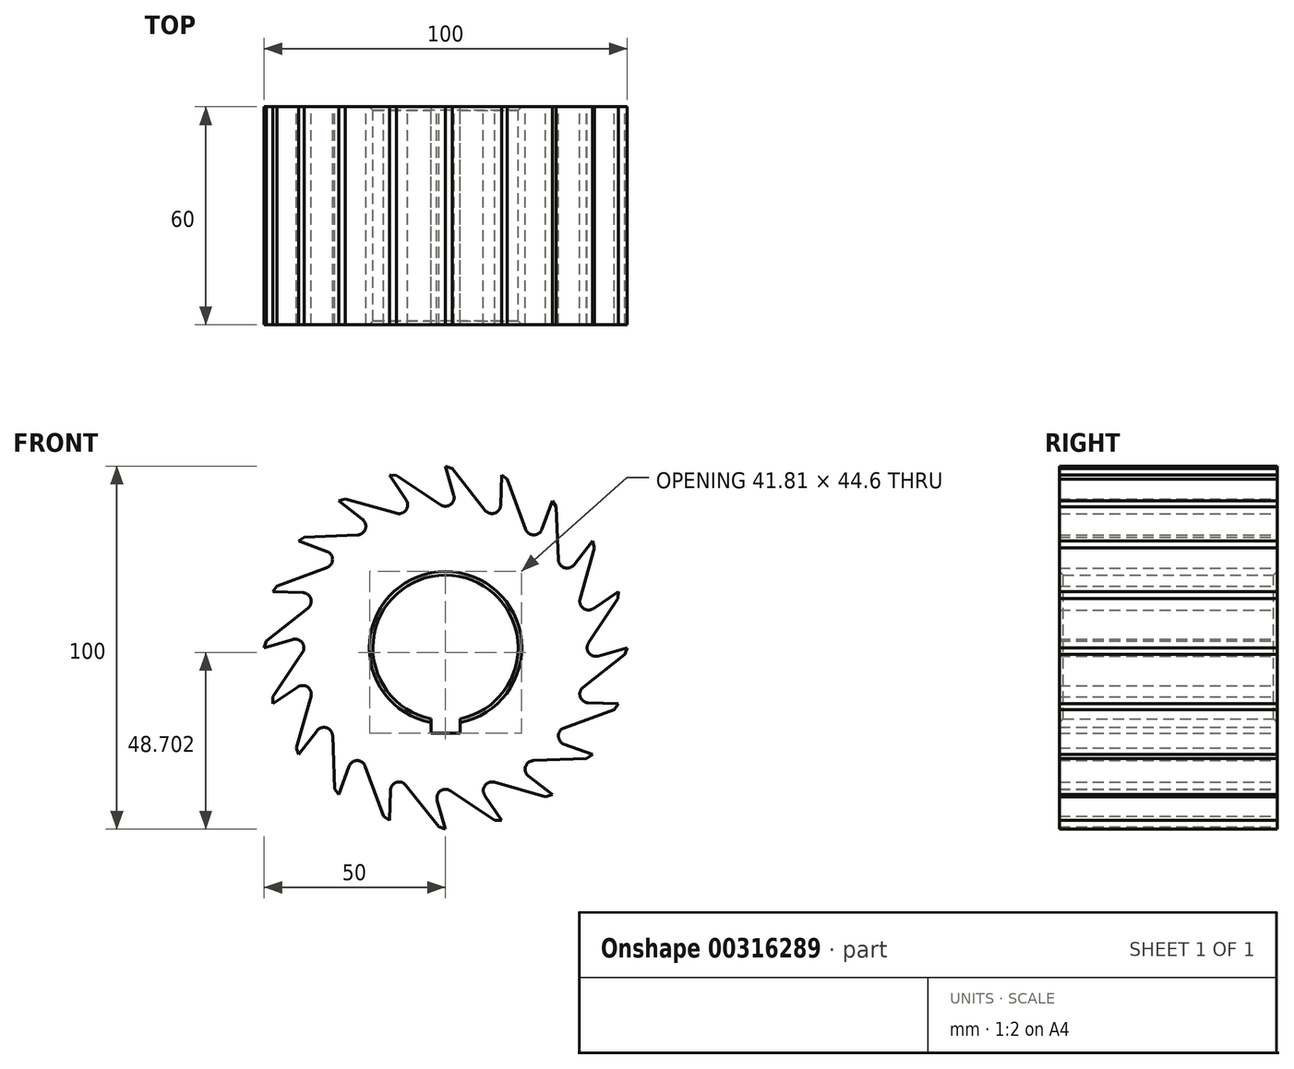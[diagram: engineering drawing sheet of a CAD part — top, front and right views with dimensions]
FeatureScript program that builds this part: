
annotation { "Feature Type Name" : "Feature", "Feature Type Description" : "" }
export const myFeature = defineFeature(function(context is Context, id is Id, definition is map)
    precondition{}
    {
        {
            var Q0;
            Q0=qCreatedBy(makeId("Front.planeOp"),FACE);
            var sketch = newSketch(context, id + "F0", { "sketchPlane" : qUnion([Q0])});
            skLineSegment(sketch, "E0", {"start": v(0, 50) * mm, "end": v(2.29, 42.02) * mm});
            skLineSegment(sketch, "E1", {"start": v(0, 50) * mm, "end": v(1.83, 49.37) * mm});
            skArc(sketch, "E2.19.0", {"start": v(10.91, 37.86) * mm, "mid": v(13.52, 37.08) * mm, "end": v(15.16, 39.26) * mm});
            skLineSegment(sketch, "E3.19.0", {"start": v(1.83, 49.37) * mm, "end": v(10.91, 37.86) * mm});
            skArc(sketch, "E4.1.0", {"start": v(-1.32, 39.38) * mm, "mid": v(1.4, 39.44) * mm, "end": v(2.29, 42.02) * mm});
            skLineSegment(sketch, "E4.1.1", {"start": v(-13.52, 47.52) * mm, "end": v(-1.32, 39.38) * mm});
            skLineSegment(sketch, "E4.1.2", {"start": v(-15.45, 47.55) * mm, "end": v(-10.8, 40.67) * mm});
            skLineSegment(sketch, "E4.1.3", {"start": v(-15.45, 47.55) * mm, "end": v(-13.52, 47.52) * mm});
            skArc(sketch, "E4.2.0", {"start": v(-13.43, 37.05) * mm, "mid": v(-10.85, 37.94) * mm, "end": v(-10.8, 40.67) * mm});
            skLineSegment(sketch, "E4.2.1", {"start": v(-27.54, 41.02) * mm, "end": v(-13.43, 37.05) * mm});
            skLineSegment(sketch, "E4.2.2", {"start": v(-29.39, 40.45) * mm, "end": v(-22.85, 35.34) * mm});
            skLineSegment(sketch, "E4.2.3", {"start": v(-29.39, 40.45) * mm, "end": v(-27.54, 41.02) * mm});
            skArc(sketch, "E4.3.0", {"start": v(-24.22, 31.09) * mm, "mid": v(-22.05, 32.73) * mm, "end": v(-22.85, 35.34) * mm});
            skLineSegment(sketch, "E4.3.1", {"start": v(-38.87, 30.5) * mm, "end": v(-24.22, 31.09) * mm});
            skLineSegment(sketch, "E4.3.2", {"start": v(-40.45, 29.39) * mm, "end": v(-32.65, 26.55) * mm});
            skLineSegment(sketch, "E4.3.3", {"start": v(-40.45, 29.39) * mm, "end": v(-38.87, 30.5) * mm});
            skArc(sketch, "E4.4.0", {"start": v(-32.64, 22.08) * mm, "mid": v(-31.08, 24.32) * mm, "end": v(-32.65, 26.55) * mm});
            skLineSegment(sketch, "E4.4.1", {"start": v(-46.39, 17) * mm, "end": v(-32.64, 22.08) * mm});
            skLineSegment(sketch, "E4.4.2", {"start": v(-47.55, 15.45) * mm, "end": v(-39.26, 15.16) * mm});
            skLineSegment(sketch, "E4.4.3", {"start": v(-47.55, 15.45) * mm, "end": v(-46.39, 17) * mm});
            skArc(sketch, "E4.5.0", {"start": v(-37.86, 10.91) * mm, "mid": v(-37.08, 13.52) * mm, "end": v(-39.26, 15.16) * mm});
            skLineSegment(sketch, "E4.5.1", {"start": v(-49.37, 1.83) * mm, "end": v(-37.86, 10.91) * mm});
            skLineSegment(sketch, "E4.5.2", {"start": v(-50, 0) * mm, "end": v(-42.02, 2.29) * mm});
            skLineSegment(sketch, "E4.5.3", {"start": v(-50, 0) * mm, "end": v(-49.37, 1.83) * mm});
            skArc(sketch, "E4.6.0", {"start": v(-39.38, -1.32) * mm, "mid": v(-39.44, 1.4) * mm, "end": v(-42.02, 2.29) * mm});
            skLineSegment(sketch, "E4.6.1", {"start": v(-47.52, -13.52) * mm, "end": v(-39.38, -1.32) * mm});
            skLineSegment(sketch, "E4.6.2", {"start": v(-47.55, -15.45) * mm, "end": v(-40.67, -10.8) * mm});
            skLineSegment(sketch, "E4.6.3", {"start": v(-47.55, -15.45) * mm, "end": v(-47.52, -13.52) * mm});
            skArc(sketch, "E4.7.0", {"start": v(-37.05, -13.43) * mm, "mid": v(-37.94, -10.85) * mm, "end": v(-40.67, -10.8) * mm});
            skLineSegment(sketch, "E4.7.1", {"start": v(-41.02, -27.54) * mm, "end": v(-37.05, -13.43) * mm});
            skLineSegment(sketch, "E4.7.2", {"start": v(-40.45, -29.39) * mm, "end": v(-35.34, -22.85) * mm});
            skLineSegment(sketch, "E4.7.3", {"start": v(-40.45, -29.39) * mm, "end": v(-41.02, -27.54) * mm});
            skArc(sketch, "E4.8.0", {"start": v(-31.09, -24.22) * mm, "mid": v(-32.73, -22.05) * mm, "end": v(-35.34, -22.85) * mm});
            skLineSegment(sketch, "E4.8.1", {"start": v(-30.5, -38.87) * mm, "end": v(-31.09, -24.22) * mm});
            skLineSegment(sketch, "E4.8.2", {"start": v(-29.39, -40.45) * mm, "end": v(-26.55, -32.65) * mm});
            skLineSegment(sketch, "E4.8.3", {"start": v(-29.39, -40.45) * mm, "end": v(-30.5, -38.87) * mm});
            skArc(sketch, "E4.9.0", {"start": v(-22.08, -32.64) * mm, "mid": v(-24.32, -31.08) * mm, "end": v(-26.55, -32.65) * mm});
            skLineSegment(sketch, "E4.9.1", {"start": v(-17, -46.39) * mm, "end": v(-22.08, -32.64) * mm});
            skLineSegment(sketch, "E4.9.2", {"start": v(-15.45, -47.55) * mm, "end": v(-15.16, -39.26) * mm});
            skLineSegment(sketch, "E4.9.3", {"start": v(-15.45, -47.55) * mm, "end": v(-17, -46.39) * mm});
            skArc(sketch, "E4.10.0", {"start": v(-10.91, -37.86) * mm, "mid": v(-13.52, -37.08) * mm, "end": v(-15.16, -39.26) * mm});
            skLineSegment(sketch, "E4.10.1", {"start": v(-1.83, -49.37) * mm, "end": v(-10.91, -37.86) * mm});
            skLineSegment(sketch, "E4.10.2", {"start": v(0, -50) * mm, "end": v(-2.29, -42.02) * mm});
            skLineSegment(sketch, "E4.10.3", {"start": v(0, -50) * mm, "end": v(-1.83, -49.37) * mm});
            skArc(sketch, "E4.11.0", {"start": v(1.32, -39.38) * mm, "mid": v(-1.4, -39.44) * mm, "end": v(-2.29, -42.02) * mm});
            skLineSegment(sketch, "E4.11.1", {"start": v(13.52, -47.52) * mm, "end": v(1.32, -39.38) * mm});
            skLineSegment(sketch, "E4.11.2", {"start": v(15.45, -47.55) * mm, "end": v(10.8, -40.67) * mm});
            skLineSegment(sketch, "E4.11.3", {"start": v(15.45, -47.55) * mm, "end": v(13.52, -47.52) * mm});
            skArc(sketch, "E4.12.0", {"start": v(13.43, -37.05) * mm, "mid": v(10.85, -37.94) * mm, "end": v(10.8, -40.67) * mm});
            skLineSegment(sketch, "E4.12.1", {"start": v(27.54, -41.02) * mm, "end": v(13.43, -37.05) * mm});
            skLineSegment(sketch, "E4.12.2", {"start": v(29.39, -40.45) * mm, "end": v(22.85, -35.34) * mm});
            skLineSegment(sketch, "E4.12.3", {"start": v(29.39, -40.45) * mm, "end": v(27.54, -41.02) * mm});
            skArc(sketch, "E4.13.0", {"start": v(24.22, -31.09) * mm, "mid": v(22.05, -32.73) * mm, "end": v(22.85, -35.34) * mm});
            skLineSegment(sketch, "E4.13.1", {"start": v(38.87, -30.5) * mm, "end": v(24.22, -31.09) * mm});
            skLineSegment(sketch, "E4.13.2", {"start": v(40.45, -29.39) * mm, "end": v(32.65, -26.55) * mm});
            skLineSegment(sketch, "E4.13.3", {"start": v(40.45, -29.39) * mm, "end": v(38.87, -30.5) * mm});
            skArc(sketch, "E4.14.0", {"start": v(32.64, -22.08) * mm, "mid": v(31.08, -24.32) * mm, "end": v(32.65, -26.55) * mm});
            skLineSegment(sketch, "E4.14.1", {"start": v(46.39, -17) * mm, "end": v(32.64, -22.08) * mm});
            skLineSegment(sketch, "E4.14.2", {"start": v(47.55, -15.45) * mm, "end": v(39.26, -15.16) * mm});
            skLineSegment(sketch, "E4.14.3", {"start": v(47.55, -15.45) * mm, "end": v(46.39, -17) * mm});
            skArc(sketch, "E4.15.0", {"start": v(37.86, -10.91) * mm, "mid": v(37.08, -13.52) * mm, "end": v(39.26, -15.16) * mm});
            skLineSegment(sketch, "E4.15.1", {"start": v(49.37, -1.83) * mm, "end": v(37.86, -10.91) * mm});
            skLineSegment(sketch, "E4.15.2", {"start": v(50, 0) * mm, "end": v(42.02, -2.29) * mm});
            skLineSegment(sketch, "E4.15.3", {"start": v(50, 0) * mm, "end": v(49.37, -1.83) * mm});
            skArc(sketch, "E4.16.0", {"start": v(39.38, 1.32) * mm, "mid": v(39.44, -1.4) * mm, "end": v(42.02, -2.29) * mm});
            skLineSegment(sketch, "E4.16.1", {"start": v(47.52, 13.52) * mm, "end": v(39.38, 1.32) * mm});
            skLineSegment(sketch, "E4.16.2", {"start": v(47.55, 15.45) * mm, "end": v(40.67, 10.8) * mm});
            skLineSegment(sketch, "E4.16.3", {"start": v(47.55, 15.45) * mm, "end": v(47.52, 13.52) * mm});
            skArc(sketch, "E4.17.0", {"start": v(37.05, 13.43) * mm, "mid": v(37.94, 10.85) * mm, "end": v(40.67, 10.8) * mm});
            skLineSegment(sketch, "E4.17.1", {"start": v(41.02, 27.54) * mm, "end": v(37.05, 13.43) * mm});
            skLineSegment(sketch, "E4.17.2", {"start": v(40.45, 29.39) * mm, "end": v(35.34, 22.85) * mm});
            skLineSegment(sketch, "E4.17.3", {"start": v(40.45, 29.39) * mm, "end": v(41.02, 27.54) * mm});
            skArc(sketch, "E4.18.0", {"start": v(31.09, 24.22) * mm, "mid": v(32.73, 22.05) * mm, "end": v(35.34, 22.85) * mm});
            skLineSegment(sketch, "E4.18.1", {"start": v(30.5, 38.87) * mm, "end": v(31.09, 24.22) * mm});
            skLineSegment(sketch, "E4.18.2", {"start": v(29.39, 40.45) * mm, "end": v(26.55, 32.65) * mm});
            skLineSegment(sketch, "E4.18.3", {"start": v(29.39, 40.45) * mm, "end": v(30.5, 38.87) * mm});
            skArc(sketch, "E4.19.0", {"start": v(22.08, 32.64) * mm, "mid": v(24.32, 31.08) * mm, "end": v(26.55, 32.65) * mm});
            skLineSegment(sketch, "E4.19.1", {"start": v(17, 46.39) * mm, "end": v(22.08, 32.64) * mm});
            skLineSegment(sketch, "E4.19.2", {"start": v(15.45, 47.55) * mm, "end": v(15.16, 39.26) * mm});
            skLineSegment(sketch, "E4.19.3", {"start": v(15.45, 47.55) * mm, "end": v(17, 46.39) * mm});
            skPoint(sketch, "E4.center", {"position": v(0, 0) * mm});
            skArc(sketch, "E5", {"start": v(4, -19.6) * mm, "mid": v(0, 20) * mm, "end": v(-4, -19.6) * mm});
            skLineSegment(sketch, "E6.top", {"start": v(4, -23.6) * mm, "end": v(-4, -23.6) * mm});
            skLineSegment(sketch, "E6.left", {"start": v(4, -19.6) * mm, "end": v(4, -23.6) * mm});
            skLineSegment(sketch, "E6.right", {"start": v(-4, -19.6) * mm, "end": v(-4, -23.6) * mm});
            skCircle(sketch, "E7", {"center": v(0, 0) * mm, "radius": 50 * mm, "construction": true});
            skSolve(sketch);
        }
        {
            var Q0;
            Q0=qSketchRegion(id+"F0",true);
            extrude(context, id + "F1", {"entities" : qUnion([Q0]), "depth" : 60 * mm});
        }
        {
            var Q0;
            Q0=makeQuery(id+"F1.opExtrude","CAP_EDGE",EDGE,{"disambiguationData":[OSD([sQuery(id+"F0.wireOp",EDGE,"E5")])],"isStart":false});
            var Q1;
            Q1=makeQuery(id+"F1.opExtrude","CAP_EDGE",EDGE,{"disambiguationData":[OSD([sQuery(id+"F0.wireOp",EDGE,"E5")])],"isStart":true});
            chamfer(context, id + "F2", {"entities" : qUnion([Q0, Q1]), "width" : 1 * mm, "tangentPropagation" : true});
        }
    });
